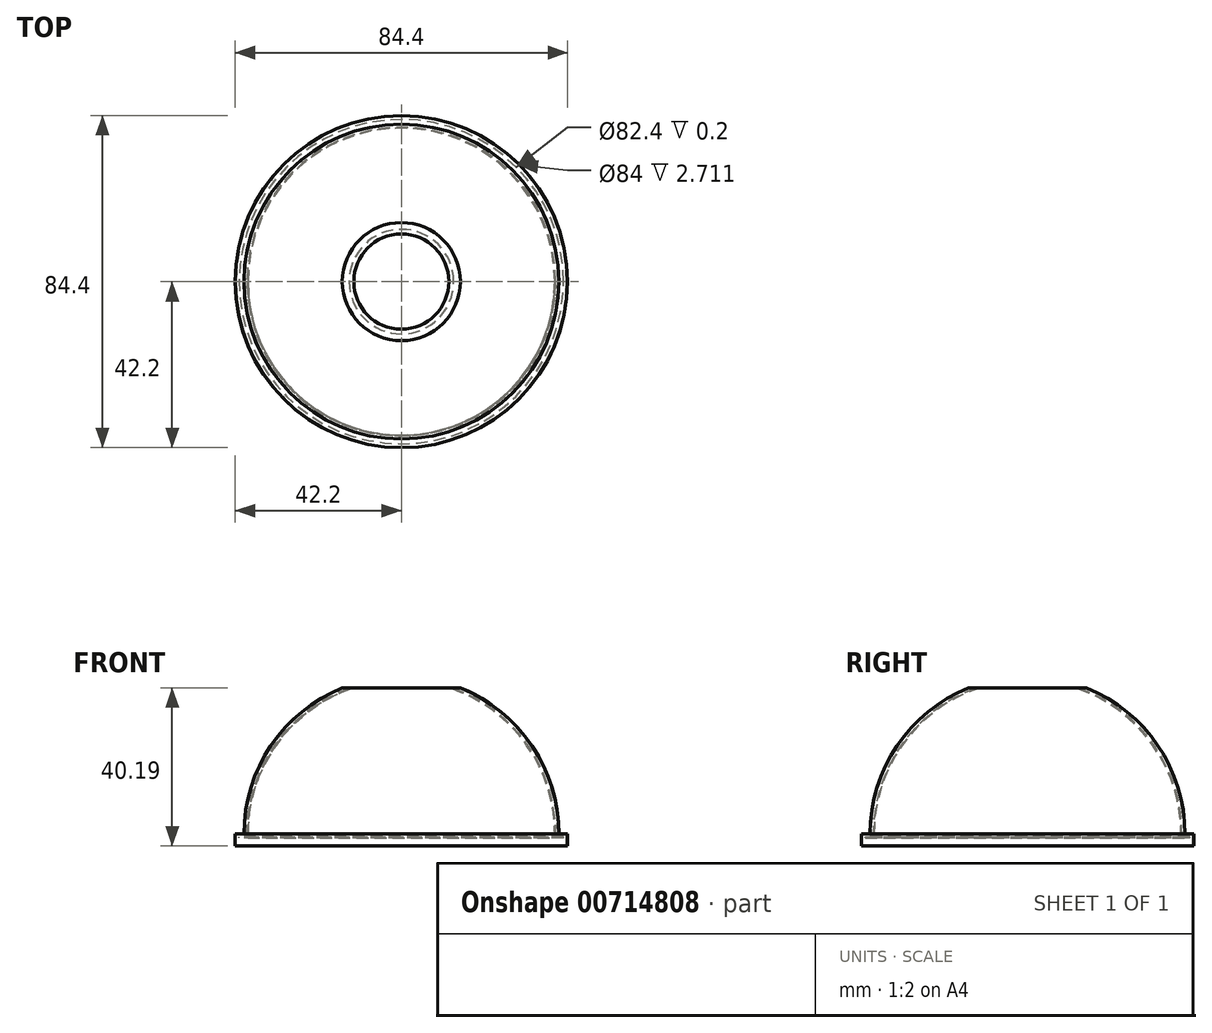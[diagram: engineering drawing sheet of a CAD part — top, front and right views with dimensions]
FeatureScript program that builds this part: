
annotation { "Feature Type Name" : "Feature", "Feature Type Description" : "" }
export const myFeature = defineFeature(function(context is Context, id is Id, definition is map)
    precondition{}
    {
        {
            var Q0;
            Q0=qCreatedBy(makeId("Right.planeOp"),FACE);
            var sketch = newSketch(context, id + "F0", { "sketchPlane" : qUnion([Q0])});
            skLineSegment(sketch, "E0", {"start": v(0, 37.08) * mm, "end": v(0, 0) * mm});
            skArc(sketch, "E1", {"start": v(40, 0) * mm, "mid": v(33.17, 22.36) * mm, "end": v(15, 37.08) * mm});
            skLineSegment(sketch, "E2", {"start": v(15, 37.08) * mm, "end": v(0, 37.08) * mm});
            skLineSegment(sketch, "E3", {"start": v(40, 0) * mm, "end": v(42.2, 0) * mm});
            skLineSegment(sketch, "E4", {"start": v(42.2, 0) * mm, "end": v(42.2, -3.11) * mm});
            skLineSegment(sketch, "E5", {"start": v(42.2, -3.11) * mm, "end": v(0, -3.11) * mm});
            skLineSegment(sketch, "E6", {"start": v(0, -3.11) * mm, "end": v(0, 0) * mm});
            skSolve(sketch);
        }
        {
            var Q0;
            Q0=qCreatedBy(makeId("Right.planeOp"),FACE);
            var sketch = newSketch(context, id + "F1", { "sketchPlane" : qUnion([Q0])});
            skLineSegment(sketch, "E7", {"start": v(0, 19.16) * mm, "end": v(0, 0) * mm});
            skSolve(sketch);
        }
        {
            var Q0;
            Q0=makeQuery(id+"F0.imprint","IMPRINT",FACE,{"disambiguationData":[TD([[makeQuery(id+"F0.imprint","IMPRINT",EDGE,{"derivedFrom":sQuery(id+"F0.wireOp",EDGE,"E0")}),1.0]])]});
            var Q1;
            Q1=sQuery(id+"F1.wireOp",EDGE,"E7");
            revolve(context, id + "F2", {"surfaceOperationType" : NewSurfaceOperationType.NEW, "entities" : qUnion([Q0]), "axis" : qUnion([Q1]), "revolveType" : RevolveType.FULL});
        }
        {
            var Q0;
            Q0=makeQuery(id+"F2.opRevolve","SWEPT_FACE",FACE,{"disambiguationData":[OSD([sQuery(id+"F0.wireOp",EDGE,"E2")])]});
            var Q1;
            Q1=makeQuery(id+"F2.opRevolve","SWEPT_FACE",FACE,{"disambiguationData":[OSD([sQuery(id+"F0.wireOp",EDGE,"E5")])]});
            shell(context, id + "F3", {"entities" : qUnion([Q0, Q1]), "thickness" : 1 * mm});
        }
        {
            var Q0;
            Q0=makeQuery(id+"F3.opShell","OFFSET_FACE",FACE,{"disambiguationData":[OSD([sQuery(id+"F0.wireOp",EDGE,"E4")])]});
            shell(context, id + "F4", {"entities" : qUnion([Q0]), "thickness" : .2 * mm});
        }
    });
